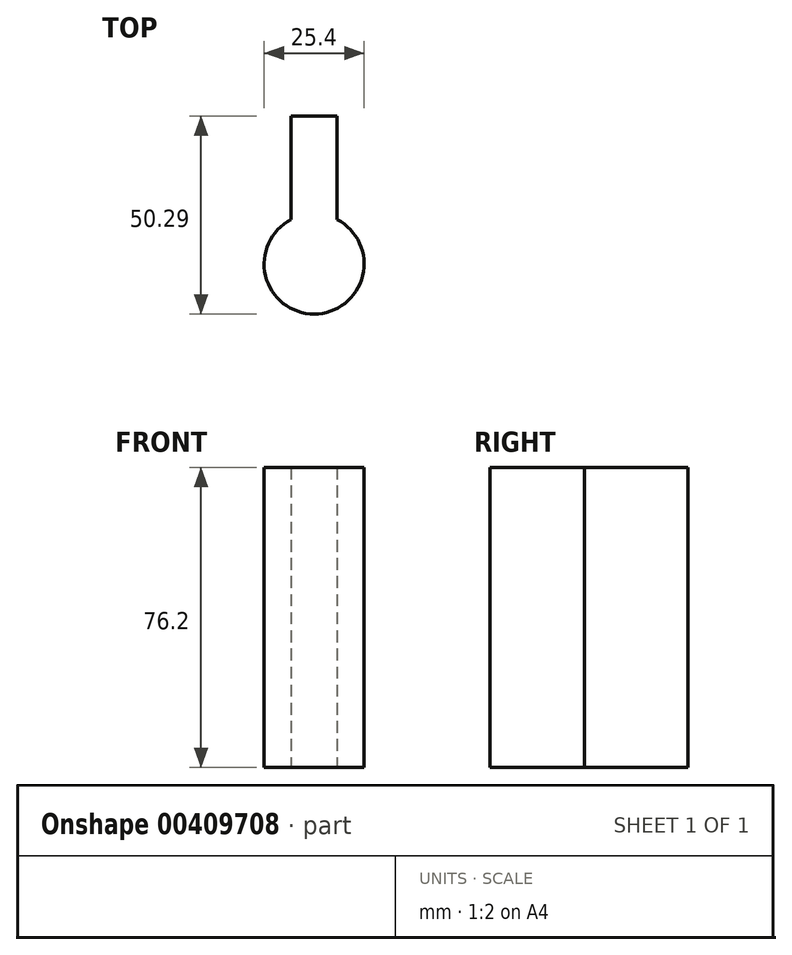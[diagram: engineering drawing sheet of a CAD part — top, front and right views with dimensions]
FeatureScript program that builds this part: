
annotation { "Feature Type Name" : "Feature", "Feature Type Description" : "" }
export const myFeature = defineFeature(function(context is Context, id is Id, definition is map)
    precondition{}
    {
        {
            var Q0;
            Q0=qCreatedBy(makeId("Top.planeOp"),FACE);
            var sketch = newSketch(context, id + "F0", { "sketchPlane" : qUnion([Q0])});
            skArc(sketch, "E0", {"start": v(-5.84, 11.28) * mm, "mid": v(0, -12.7) * mm, "end": v(5.84, 11.28) * mm});
            skLineSegment(sketch, "E1", {"start": v(-5.84, 11.28) * mm, "end": v(-5.84, 37.6) * mm});
            skLineSegment(sketch, "E2", {"start": v(-5.84, 37.6) * mm, "end": v(5.84, 37.6) * mm});
            skLineSegment(sketch, "E3", {"start": v(5.84, 37.6) * mm, "end": v(5.84, 11.28) * mm});
            skSolve(sketch);
        }
        {
            var Q0;
            Q0 = qSketchRegion(id + "F0", true);
            extrude(context, id + "F1", {"entities" : qUnion([Q0]), "depth" : 76.2 * mm});
        }
        {
            var Q0;
            Q0=makeQuery(id+"F1.opExtrude","SWEPT_FACE",FACE,{"disambiguationData":[OSD([sQuery(id+"F0.wireOp",EDGE,"E3")])]});
            var sketch = newSketch(context, id + "F2", { "sketchPlane" : qUnion([Q0])});
            skSolve(sketch);
        }
        {
            var Q0;
            {var subQ0=sQuery(id+"F0.wireOp",EDGE,"E3");Q0=makeQuery(id+"F2.imprint","IMPRINT",FACE,{"disambiguationData":[TD([[makeQuery(id+"F2.imprint","IMPRINT",EDGE,{"derivedFrom":makeQuery(id+"F1.opExtrude","CAP_EDGE",EDGE,{"disambiguationData":[OSD([subQ0])],"isStart":true})}),-1.0]])]});}
            var sketch = newSketch(context, id + "F3", { "sketchPlane" : qUnion([Q0])});
            skLineSegment(sketch, "E4", {"start": v(27.7, 28.09) * mm, "end": v(0, -45.71) * mm});
            skLineSegment(sketch, "E5", {"start": v(0, -45.71) * mm, "end": v(45.12, -39.42) * mm});
            skLineSegment(sketch, "E6", {"start": v(45.12, -39.42) * mm, "end": v(30.65, -51.05) * mm});
            skLineSegment(sketch, "E7", {"start": v(30.65, -51.05) * mm, "end": v(26.36, -81.61) * mm});
            skLineSegment(sketch, "E8", {"start": v(26.36, -81.61) * mm, "end": v(-21.27, -78.92) * mm});
            skLineSegment(sketch, "E9", {"start": v(-21.27, -78.92) * mm, "end": v(-27.01, -25.4) * mm});
            skLineSegment(sketch, "E10", {"start": v(-27.01, -25.4) * mm, "end": v(9, -6.87) * mm});
            skLineSegment(sketch, "E11", {"start": v(9, -6.87) * mm, "end": v(7.16, 22.18) * mm});
            skLineSegment(sketch, "E12", {"start": v(7.16, 22.18) * mm, "end": v(27.7, 28.09) * mm});
            skSolve(sketch);
        }
        {
            var Q0;
            Q0 = qSketchRegion(id + "F3", true);
            var Q1;
            Q1=sQuery(id+"F3.wireOp",EDGE,"E7");
            var Q2;
            Q2=sQuery(id+"F3.wireOp",EDGE,"E4");
            var Q3;
            Q3=sQuery(id+"F3.wireOp",EDGE,"E8");
            var Q4;
            Q4=sQuery(id+"F3.wireOp",EDGE,"E9");
            var Q5;
            Q5=sQuery(id+"F3.wireOp",EDGE,"E10");
            var Q6;
            Q6=sQuery(id+"F3.wireOp",EDGE,"E5");
            var Q7;
            Q7=sQuery(id+"F3.wireOp",EDGE,"E6");
            var Q8;
            Q8=sQuery(id+"F3.wireOp",EDGE,"E11");
            var Q9;
            Q9=sQuery(id+"F3.wireOp",EDGE,"E12");
            extrude(context, id + "F4", {"entities" : qUnion([Q0]), "bodyType" : ToolBodyType.SURFACE, "surfaceEntities" : qUnion([Q1, Q2, Q3, Q4, Q5, Q6, Q7, Q8, Q9]), "endBound" : BoundingType.SYMMETRIC, "depth" : 25.4 * mm});
        }
        {
            var Q0;
            Q0=makeQuery(id+"F4.opExtrude","CAP_VERTEX",VERTEX,{"disambiguationData":[OSD([sQuery(id+"F3.wireOp",VERTEX,"E10.start")])],"isStart":false});
            var Q1;
            Q1=makeQuery(id+"F4.opExtrude","CAP_VERTEX",VERTEX,{"disambiguationData":[OSD([sQuery(id+"F3.wireOp",VERTEX,"E11.start")])],"isStart":false});
            var Q2;
            Q2=makeQuery(id+"F4.opExtrude","CAP_VERTEX",VERTEX,{"disambiguationData":[OSD([sQuery(id+"F3.wireOp",VERTEX,"E5.start")])],"isStart":false});
            cPlane(context, id + "F5", {"entities" : qUnion([Q0, Q1, Q2]), "cplaneType" : CPlaneType.THREE_POINT, "offset" : 25.4 * mm, "width" : 152.4 * mm, "height" : 152.4 * mm});
        }
    });
